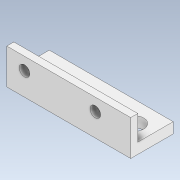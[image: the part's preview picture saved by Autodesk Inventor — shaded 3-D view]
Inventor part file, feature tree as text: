
AUTODESK INVENTOR PART (.ipt)
format: ipt  version: 2022 (Build 260153000, 153)  size: 151,552 bytes
history: native  units: mm
features: extrude x5, sketch x5, projected_geometry x2
ambient origin geometry x8: Origin, YZ Plane, XZ Plane, XY Plane, X Axis, Y Axis, Z Axis, Center Point
bodies: Solid1 (feature_tree)
feature tree (12):
  extrude  "Extrusion1"  Depth=50.0mm
  extrude  "Extrusion2"  Depth=5.5mm
  extrude  "Extrusion3"  Depth=7.0mm TaperAngle=0.0deg
  extrude  "Extrusion4"  TaperAngle=0.0deg  [1 undecoded]
  extrude  "Extrusion5"  Depth=10.0mm
  sketch  "Sketch1"  dims[d0=25.0mm d1=50.0mm]
  sketch  "Sketch2"  dims[d2=5.5mm d3=5.5mm]
  sketch  "Sketch3"  dims[d4=3.0mm d5=0.0mm d6=7.0mm d7=0.0mm]
  sketch  "Sketch4"  dims[d8=30.0mm d9=0.0mm]
  projected_geometry  "Projected Loop1"
  sketch  "Sketch5"  dims[d10=3.5mm d11=10.0mm d12=20.0mm d13=3.0mm d14=3.0mm d15=10.0mm d16=0.0mm d17=10.0mm d18=0.0mm d19=5.0mm d20=0.0mm]
  projected_geometry  "Projected Loop2"
note: 1 required parameter value undecoded (feature->parameter linkage not recoverable at this tier; creation-order binding heuristic only, values carry confidence <= 0.55)
